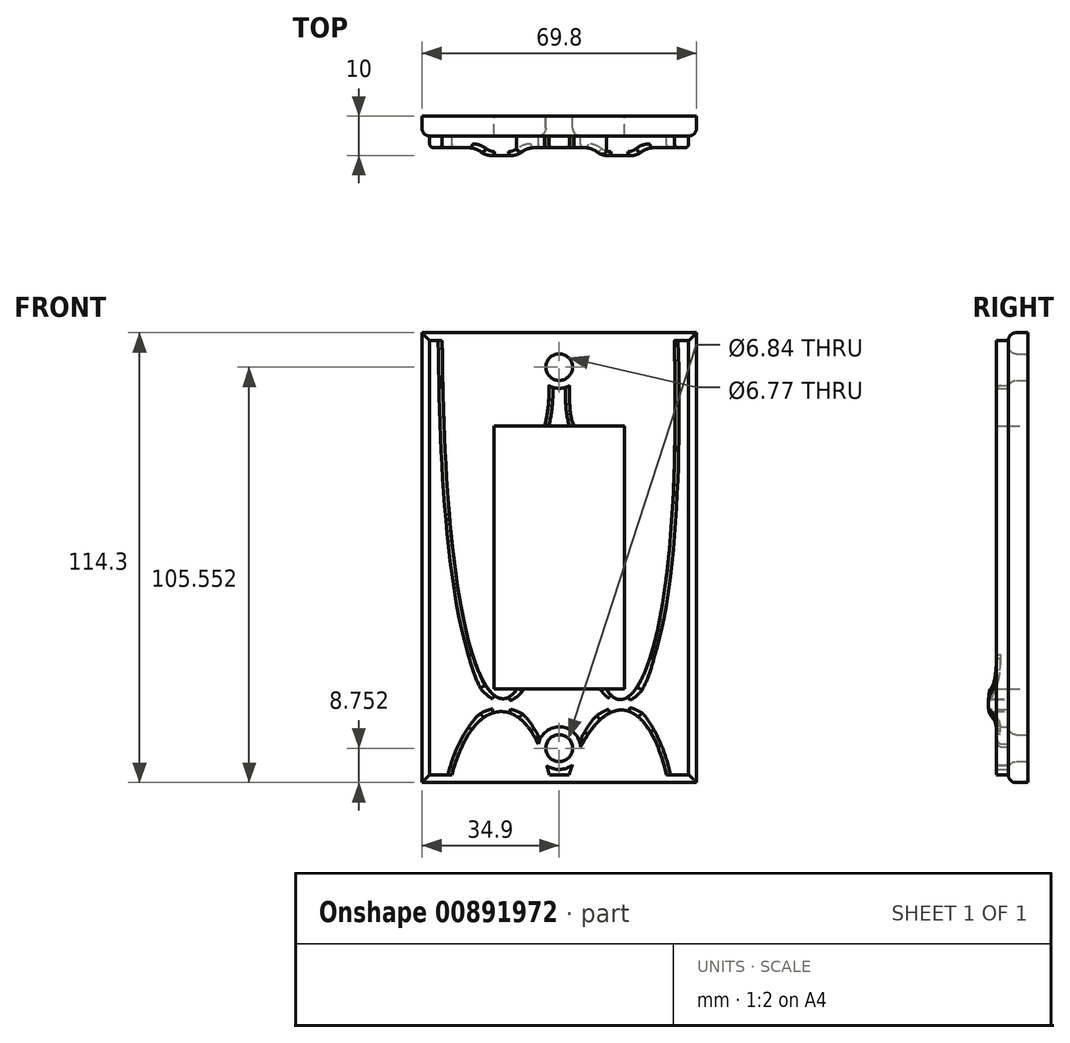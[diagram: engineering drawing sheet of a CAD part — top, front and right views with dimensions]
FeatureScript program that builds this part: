
annotation { "Feature Type Name" : "Feature", "Feature Type Description" : "" }
export const myFeature = defineFeature(function(context is Context, id is Id, definition is map)
    precondition{}
    {
        {
            var Q0;
            Q0=qCreatedBy(makeId("Front.planeOp"),FACE);
            var sketch = newSketch(context, id + "F0", { "sketchPlane" : qUnion([Q0])});
            skLineSegment(sketch, "E0.bottom", {"start": v(-34.9, 67.2) * mm, "end": v(34.9, 67.2) * mm});
            skLineSegment(sketch, "E0.top", {"start": v(-34.9, -47.1) * mm, "end": v(34.9, -47.1) * mm});
            skLineSegment(sketch, "E0.left", {"start": v(-34.9, 67.2) * mm, "end": v(-34.9, -47.1) * mm});
            skLineSegment(sketch, "E0.right", {"start": v(34.9, 67.2) * mm, "end": v(34.9, -47.1) * mm});
            skLineSegment(sketch, "E1", {"start": v(34.9, 67.2) * mm, "end": v(0, 67.2) * mm, "construction": true});
            skLineSegment(sketch, "E2", {"start": v(34.9, 67.2) * mm, "end": v(34.9, 10.05) * mm, "construction": true});
            skLineSegment(sketch, "E3", {"start": v(34.9, 10.05) * mm, "end": v(-34.9, 10.05) * mm, "construction": true});
            skLineSegment(sketch, "E4", {"start": v(-34.9, 10.05) * mm, "end": v(0, 10.05) * mm, "construction": true});
            skLineSegment(sketch, "E5", {"start": v(0, 10.05) * mm, "end": v(0, -47.1) * mm, "construction": true});
            skLineSegment(sketch, "E6", {"start": v(0, -47.1) * mm, "end": v(0, 67.2) * mm, "construction": true});
            skLineSegment(sketch, "E7", {"start": v(0, 10.05) * mm, "end": v(0, 58.45) * mm, "construction": true});
            skLineSegment(sketch, "E8", {"start": v(0, 10.05) * mm, "end": v(0, -38.35) * mm, "construction": true});
            skCircle(sketch, "E9", {"center": v(0, -38.35) * mm, "radius": 3.42 * mm});
            skCircle(sketch, "E10", {"center": v(0, 58.45) * mm, "radius": 3.39 * mm});
            skLineSegment(sketch, "E11.bottom", {"start": v(-16.6, 43.45) * mm, "end": v(16.6, 43.45) * mm});
            skLineSegment(sketch, "E11.top", {"start": v(-16.6, -23.35) * mm, "end": v(16.6, -23.35) * mm});
            skLineSegment(sketch, "E11.left", {"start": v(-16.6, 43.45) * mm, "end": v(-16.6, -23.35) * mm});
            skLineSegment(sketch, "E11.right", {"start": v(16.6, 43.45) * mm, "end": v(16.6, -23.35) * mm});
            skSolve(sketch);
        }
        {
            var Q0;
            Q0=makeQuery(id+"F0.imprint","IMPRINT",FACE,{"disambiguationData":[TD([[makeQuery(id+"F0.imprint","IMPRINT",EDGE,{"derivedFrom":sQuery(id+"F0.wireOp",EDGE,"E0.bottom")}),-1.0]])]});
            extrude(context, id + "F1", {"entities" : qUnion([Q0]), "depth" : 5 * mm, "offsetDistance" : 25 * mm});
        }
        {
            var Q0;
            Q0=makeQuery(id+"F1.opExtrude","CAP_EDGE",EDGE,{"disambiguationData":[OSD([sQuery(id+"F0.wireOp",EDGE,"E0.left")])],"isStart":false});
            var Q1;
            Q1=makeQuery(id+"F1.opExtrude","CAP_EDGE",EDGE,{"disambiguationData":[OSD([sQuery(id+"F0.wireOp",EDGE,"E0.top")])],"isStart":false});
            var Q2;
            Q2=makeQuery(id+"F1.opExtrude","CAP_EDGE",EDGE,{"disambiguationData":[OSD([sQuery(id+"F0.wireOp",EDGE,"E0.right")])],"isStart":false});
            var Q3;
            Q3=makeQuery(id+"F1.opExtrude","CAP_EDGE",EDGE,{"disambiguationData":[OSD([sQuery(id+"F0.wireOp",EDGE,"E0.bottom")])],"isStart":false});
            var Q4;
            Q4=makeQuery(id+"F1.opExtrude","CAP_EDGE",EDGE,{"disambiguationData":[OSD([sQuery(id+"F0.wireOp",EDGE,"E10")])],"isStart":false});
            var Q5;
            Q5=makeQuery(id+"F1.opExtrude","CAP_EDGE",EDGE,{"disambiguationData":[OSD([sQuery(id+"F0.wireOp",EDGE,"E9")])],"isStart":false});
            fillet(context, id + "F2", {"entities" : qUnion([Q0, Q1, Q2, Q3, Q4, Q5]), "radius" : 2 * mm, "tangentPropagation" : true, "allowEdgeOverflow" : false});
        }
        {
            var Q0;
            Q0=makeQuery(id+"F1.opExtrude","CAP_FACE",FACE,{"disambiguationData":[OSD([sQuery(id+"F0.wireOp",EDGE,"E0.bottom"),sQuery(id+"F0.wireOp",EDGE,"E0.top"),sQuery(id+"F0.wireOp",EDGE,"E0.left"),sQuery(id+"F0.wireOp",EDGE,"E0.right"),sQuery(id+"F0.wireOp",EDGE,"E9"),sQuery(id+"F0.wireOp",EDGE,"E10"),sQuery(id+"F0.wireOp",EDGE,"E11.bottom"),sQuery(id+"F0.wireOp",EDGE,"E11.top"),sQuery(id+"F0.wireOp",EDGE,"E11.left"),sQuery(id+"F0.wireOp",EDGE,"E11.right")])],"isStart":false});
            var sketch = newSketch(context, id + "F3", { "sketchPlane" : qUnion([Q0])});
            skLineSegment(sketch, "E12", {"start": v(-33.36, 65.88) * mm, "end": v(-32.9, -45.1) * mm});
            skLineSegment(sketch, "E13", {"start": v(-32.9, -45.1) * mm, "end": v(32.9, -45.1) * mm});
            skLineSegment(sketch, "E14", {"start": v(32.9, -45.1) * mm, "end": v(32.91, 64.93) * mm});
            skPoint(sketch, "E15.2.internal.snap0", {"position": v(0, 43.45) * mm});
            skFitSpline(sketch, "E16", {"points": [v(0, 53.07) * mm, v(15.96, -25.97) * mm, v(29.23, 65.2) * mm], "startDerivative": vector(30.16, -374.7) * mm, "endDerivative": vector(-10.17, 378.6) * mm});
            skFitSpline(sketch, "E17", {"points": [v(-29.73, 65.2) * mm, v(-14.8, -25.74) * mm, v(0, 53.07) * mm], "startDerivative": vector(3.07, -378.06) * mm, "endDerivative": vector(19.08, 378.27) * mm});
            skFitSpline(sketch, "E18", {"points": [v(-27.27, -45.1) * mm, v(-14.8, -29.05) * mm, v(-2.5, -45.1) * mm], "startDerivative": vector(17.97, 66.24) * mm, "endDerivative": vector(18.22, -67.46) * mm});
            skFitSpline(sketch, "E19", {"points": [v(27.28, -45.1) * mm, v(15.96, -28.65) * mm, v(2.5, -45.1) * mm], "startDerivative": vector(-14.59, 62.05) * mm, "endDerivative": vector(-20.48, -61.71) * mm});
            skFitSpline(sketch, "E20", {"points": [v(-3.8, 43.45) * mm, v(-2.61, 53.74) * mm], "startDerivative": vector(2.25, 5.58) * mm, "endDerivative": vector(-0.52, 10.92) * mm});
            skFitSpline(sketch, "E21", {"points": [v(3.8, 43.45) * mm, v(2.61, 53.74) * mm], "startDerivative": vector(-3.3, 6.36) * mm, "endDerivative": vector(0.26, 12.75) * mm});
            skSolve(sketch);
        }
        {
            var Q0;
            {var subQ9=sQuery(id+"F3.wireOp",EDGE,"E14");Q0=makeQuery(id+"F3.imprint","IMPRINT",FACE,{"disambiguationData":[TD([[makeQuery(id+"F3.imprint","IMPRINT",EDGE,{"derivedFrom":subQ9}),1.0]])]});}
            var Q1;
            {var subQ0=sQuery(id+"F3.wireOp",EDGE,"E18");var subQ1=sQuery(id+"F3.wireOp",EDGE,"E13");var subQ2=makeQuery(id+"F3.imprint","INTERSECT",VERTEX,{"disambiguationData":[OD(1.0)],"derivedFrom":[subQ1,subQ0]});Q1=makeQuery(id+"F3.imprint","IMPRINT",FACE,{"disambiguationData":[TD([[makeQuery(id+"F3.imprint","IMPRINT",EDGE,{"disambiguationData":[TD([[subQ2,-1.0]])],"derivedFrom":subQ1}),1.0]])]});}
            var Q2;
            {var subQ0=sQuery(id+"F0.wireOp",EDGE,"E11.top");var subQ10=sQuery(id+"F3.wireOp",EDGE,"E16");var subQ11=makeQuery(id+"F1.opExtrude","CAP_EDGE",EDGE,{"disambiguationData":[OSD([subQ0])],"isStart":false});var subQ12=makeQuery(id+"F3.imprint","INTERSECT",VERTEX,{"derivedFrom":[subQ11,subQ10]});Q2=makeQuery(id+"F3.imprint","IMPRINT",FACE,{"disambiguationData":[TD([[makeQuery(id+"F3.imprint","IMPRINT",EDGE,{"disambiguationData":[TD([[subQ12,1.0]])],"derivedFrom":subQ11}),-1.0]])]});}
            var Q3;
            {var subQ7=sQuery(id+"F3.wireOp",EDGE,"E20");Q3=makeQuery(id+"F3.imprint","IMPRINT",FACE,{"disambiguationData":[TD([[makeQuery(id+"F3.imprint","IMPRINT",EDGE,{"derivedFrom":subQ7}),-1.0]])]});}
            var Q4;
            {var subQ7=sQuery(id+"F3.wireOp",EDGE,"E21");Q4=makeQuery(id+"F3.imprint","IMPRINT",FACE,{"disambiguationData":[TD([[makeQuery(id+"F3.imprint","IMPRINT",EDGE,{"derivedFrom":subQ7}),1.0]])]});}
            var Q5;
            {var subQ1=sQuery(id+"F3.wireOp",EDGE,"E16");var subQ2=sQuery(id+"F0.wireOp",EDGE,"E11.bottom");var subQ5=makeQuery(id+"F1.opExtrude","CAP_EDGE",EDGE,{"disambiguationData":[OSD([subQ2])],"isStart":false});var subQ6=makeQuery(id+"F3.imprint","INTERSECT",VERTEX,{"derivedFrom":[subQ5,subQ1]});Q5=makeQuery(id+"F3.imprint","IMPRINT",FACE,{"disambiguationData":[TD([[makeQuery(id+"F3.imprint","IMPRINT",EDGE,{"disambiguationData":[TD([[subQ6,1.0]])],"derivedFrom":subQ5}),1.0]])]});}
            extrude(context, id + "F4", {"entities" : qUnion([Q0, Q1, Q2, Q3, Q4, Q5]), "operationType" : NewBodyOperationType.ADD, "depth" : 3 * mm, "offsetDistance" : 25 * mm});
        }
        {
            var Q0;
            Q0=makeQuery(id+"F4.opExtrude","CAP_FACE",FACE,{"disambiguationData":[OSD([sQuery(id+"F0.wireOp",EDGE,"E0.bottom"),sQuery(id+"F0.wireOp",EDGE,"E0.top"),sQuery(id+"F0.wireOp",EDGE,"E0.left"),sQuery(id+"F0.wireOp",EDGE,"E0.right"),sQuery(id+"F0.wireOp",EDGE,"E9"),sQuery(id+"F0.wireOp",EDGE,"E10"),sQuery(id+"F0.wireOp",EDGE,"E11.bottom"),sQuery(id+"F0.wireOp",EDGE,"E11.top"),sQuery(id+"F0.wireOp",EDGE,"E11.left"),sQuery(id+"F0.wireOp",EDGE,"E11.right"),sQuery(id+"F3.wireOp",EDGE,"E13"),sQuery(id+"F3.wireOp",EDGE,"E16"),sQuery(id+"F3.wireOp",EDGE,"E17"),sQuery(id+"F3.wireOp",EDGE,"E18"),sQuery(id+"F3.wireOp",EDGE,"E19")])],"isStart":false});
            var sketch = newSketch(context, id + "F5", { "sketchPlane" : qUnion([Q0])});
            skLineSegment(sketch, "E22", {"start": v(-24.07, -6.77) * mm, "end": v(-24.07, -36.63) * mm});
            skLineSegment(sketch, "E23", {"start": v(-5.31, -37.28) * mm, "end": v(-5.31, -23.35) * mm});
            skLineSegment(sketch, "E24", {"start": v(5.41, -38.06) * mm, "end": v(5.41, -23.35) * mm});
            skLineSegment(sketch, "E25", {"start": v(25.07, -38.06) * mm, "end": v(25.07, -7.85) * mm});
            skSolve(sketch);
        }
        {
            var Q0;
            Q0 = qSketchRegion(id + "F5", true);
            var Q1;
            {var subQ4=sQuery(id+"F5.wireOp",EDGE,"E22");Q1=makeQuery(id+"F5.imprint","IMPRINT",FACE,{"disambiguationData":[TD([[makeQuery(id+"F5.imprint","IMPRINT",EDGE,{"derivedFrom":subQ4}),1.0]])]});}
            var Q2;
            {var subQ0=sQuery(id+"F5.wireOp",EDGE,"E24");Q2=makeQuery(id+"F5.imprint","IMPRINT",FACE,{"disambiguationData":[TD([[makeQuery(id+"F5.imprint","IMPRINT",EDGE,{"derivedFrom":subQ0}),-1.0]])]});}
            extrude(context, id + "F6", {"entities" : qUnion([Q0, Q1, Q2]), "operationType" : NewBodyOperationType.ADD, "depth" : 2 * mm, "offsetDistance" : 25 * mm});
        }
        {
            var Q0;
            Q0=makeQuery(id+"F6.opExtrude","CAP_EDGE",EDGE,{"disambiguationData":[OSD([sQuery(id+"F5.wireOp",EDGE,"E22")])],"isStart":false});
            var Q1;
            Q1=makeQuery(id+"F6.opExtrude","CAP_EDGE",EDGE,{"disambiguationData":[OSD([sQuery(id+"F5.wireOp",EDGE,"E23")])],"isStart":false});
            var Q2;
            Q2=makeQuery(id+"F6.opExtrude","CAP_EDGE",EDGE,{"disambiguationData":[OSD([sQuery(id+"F5.wireOp",EDGE,"E24")])],"isStart":false});
            var Q3;
            Q3=makeQuery(id+"F6.opExtrude","CAP_EDGE",EDGE,{"disambiguationData":[OSD([sQuery(id+"F5.wireOp",EDGE,"E25")])],"isStart":false});
            chamfer(context, id + "F7", {"entities" : qUnion([Q0, Q1, Q2, Q3]), "width" : 5 * mm, "tangentPropagation" : true});
        }
        {
            var Q0;
            {var subQ0=sQuery(id+"F5.wireOp",EDGE,"E22");Q0=makeQuery(id+"F7.opChamfer","BLEND_EDGE",EDGE,{"blendedFrom":[makeQuery(id+"F6.opExtrude","CAP_EDGE",EDGE,{"disambiguationData":[OSD([subQ0])],"isStart":false}),makeQuery(id+"F6.opExtrude","CAP_FACE",FACE,{"disambiguationData":[OSD([sQuery(id+"F0.wireOp",EDGE,"E11.top"),sQuery(id+"F3.wireOp",EDGE,"E17"),sQuery(id+"F3.wireOp",EDGE,"E18"),subQ0,sQuery(id+"F5.wireOp",EDGE,"E23")])],"isStart":false})],"blendedInto":[makeQuery(id+"F6.opExtrude","CAP_FACE",FACE,{"disambiguationData":[OSD([sQuery(id+"F0.wireOp",EDGE,"E11.top"),sQuery(id+"F3.wireOp",EDGE,"E17"),sQuery(id+"F3.wireOp",EDGE,"E18"),subQ0,sQuery(id+"F5.wireOp",EDGE,"E23")])],"isStart":false})]});}
            var Q1;
            {var subQ0=sQuery(id+"F5.wireOp",EDGE,"E23");Q1=makeQuery(id+"F7.opChamfer","BLEND_EDGE",EDGE,{"blendedFrom":[makeQuery(id+"F6.opExtrude","CAP_EDGE",EDGE,{"disambiguationData":[OSD([subQ0])],"isStart":false}),makeQuery(id+"F6.opExtrude","CAP_FACE",FACE,{"disambiguationData":[OSD([sQuery(id+"F0.wireOp",EDGE,"E11.top"),sQuery(id+"F3.wireOp",EDGE,"E17"),sQuery(id+"F3.wireOp",EDGE,"E18"),sQuery(id+"F5.wireOp",EDGE,"E22"),subQ0])],"isStart":false})],"blendedInto":[makeQuery(id+"F6.opExtrude","CAP_FACE",FACE,{"disambiguationData":[OSD([sQuery(id+"F0.wireOp",EDGE,"E11.top"),sQuery(id+"F3.wireOp",EDGE,"E17"),sQuery(id+"F3.wireOp",EDGE,"E18"),sQuery(id+"F5.wireOp",EDGE,"E22"),subQ0])],"isStart":false})]});}
            var Q2;
            {var subQ0=sQuery(id+"F5.wireOp",EDGE,"E24");Q2=makeQuery(id+"F7.opChamfer","BLEND_EDGE",EDGE,{"blendedFrom":[makeQuery(id+"F6.opExtrude","CAP_EDGE",EDGE,{"disambiguationData":[OSD([subQ0])],"isStart":false}),makeQuery(id+"F6.opExtrude","CAP_FACE",FACE,{"disambiguationData":[OSD([sQuery(id+"F0.wireOp",EDGE,"E11.top"),sQuery(id+"F3.wireOp",EDGE,"E16"),sQuery(id+"F3.wireOp",EDGE,"E19"),subQ0,sQuery(id+"F5.wireOp",EDGE,"E25")])],"isStart":false})],"blendedInto":[makeQuery(id+"F6.opExtrude","CAP_FACE",FACE,{"disambiguationData":[OSD([sQuery(id+"F0.wireOp",EDGE,"E11.top"),sQuery(id+"F3.wireOp",EDGE,"E16"),sQuery(id+"F3.wireOp",EDGE,"E19"),subQ0,sQuery(id+"F5.wireOp",EDGE,"E25")])],"isStart":false})]});}
            var Q3;
            {var subQ0=sQuery(id+"F5.wireOp",EDGE,"E25");Q3=makeQuery(id+"F7.opChamfer","BLEND_EDGE",EDGE,{"blendedFrom":[makeQuery(id+"F6.opExtrude","CAP_EDGE",EDGE,{"disambiguationData":[OSD([subQ0])],"isStart":false}),makeQuery(id+"F6.opExtrude","CAP_FACE",FACE,{"disambiguationData":[OSD([sQuery(id+"F0.wireOp",EDGE,"E11.top"),sQuery(id+"F3.wireOp",EDGE,"E16"),sQuery(id+"F3.wireOp",EDGE,"E19"),sQuery(id+"F5.wireOp",EDGE,"E24"),subQ0])],"isStart":false})],"blendedInto":[makeQuery(id+"F6.opExtrude","CAP_FACE",FACE,{"disambiguationData":[OSD([sQuery(id+"F0.wireOp",EDGE,"E11.top"),sQuery(id+"F3.wireOp",EDGE,"E16"),sQuery(id+"F3.wireOp",EDGE,"E19"),sQuery(id+"F5.wireOp",EDGE,"E24"),subQ0])],"isStart":false})]});}
            fillet(context, id + "F8", {"entities" : qUnion([Q0, Q1, Q2, Q3]), "radius" : 5 * mm, "tangentPropagation" : true, "allowEdgeOverflow" : false});
        }
        {
            var Q0;
            {var subQ0=sQuery(id+"F0.wireOp",EDGE,"E11.right");var subQ1=sQuery(id+"F0.wireOp",EDGE,"E11.left");var subQ2=sQuery(id+"F0.wireOp",EDGE,"E11.top");var subQ3=sQuery(id+"F0.wireOp",EDGE,"E11.bottom");var subQ4=sQuery(id+"F0.wireOp",EDGE,"E10");var subQ5=sQuery(id+"F0.wireOp",EDGE,"E9");var subQ6=sQuery(id+"F0.wireOp",EDGE,"E0.right");var subQ7=sQuery(id+"F0.wireOp",EDGE,"E0.left");var subQ8=sQuery(id+"F0.wireOp",EDGE,"E0.top");var subQ9=sQuery(id+"F0.wireOp",EDGE,"E0.bottom");var subQ12=sQuery(id+"F3.wireOp",EDGE,"E18");var subQ13=sQuery(id+"F3.wireOp",EDGE,"E13");var subQ15=sQuery(id+"F3.wireOp",EDGE,"E17");var subQ17=sQuery(id+"F5.wireOp",EDGE,"E22");Q0=makeQuery(id+"F7.opChamfer","BLEND_EDGE",EDGE,{"blendedFrom":[makeQuery(id+"F6.opExtrude","CAP_EDGE",EDGE,{"disambiguationData":[OSD([subQ17])],"isStart":false}),makeQuery(id+"F6.boolean.opBoolean","SPLIT",FACE,{"disambiguationData":[TD([makeQuery(id+"F4.opExtrude","SWEPT_FACE",FACE,{"disambiguationData":[OSD([subQ15])]})])],"derivedFrom":makeQuery(id+"F4.opExtrude","CAP_FACE",FACE,{"disambiguationData":[OSD([subQ9,subQ8,subQ7,subQ6,subQ5,subQ4,subQ3,subQ2,subQ1,subQ0,subQ13,sQuery(id+"F3.wireOp",EDGE,"E16"),subQ15,subQ12,sQuery(id+"F3.wireOp",EDGE,"E19")])],"isStart":false})})],"blendedInto":[makeQuery(id+"F6.boolean.opBoolean","SPLIT",FACE,{"disambiguationData":[TD([makeQuery(id+"F4.opExtrude","SWEPT_FACE",FACE,{"disambiguationData":[OSD([subQ15])]})])],"derivedFrom":makeQuery(id+"F4.opExtrude","CAP_FACE",FACE,{"disambiguationData":[OSD([subQ9,subQ8,subQ7,subQ6,subQ5,subQ4,subQ3,subQ2,subQ1,subQ0,subQ13,sQuery(id+"F3.wireOp",EDGE,"E16"),subQ15,subQ12,sQuery(id+"F3.wireOp",EDGE,"E19")])],"isStart":false})})]});}
            var Q1;
            {var subQ0=sQuery(id+"F0.wireOp",EDGE,"E11.top");var subQ2=sQuery(id+"F3.wireOp",EDGE,"E16");var subQ4=sQuery(id+"F3.wireOp",EDGE,"E19");var subQ5=sQuery(id+"F3.wireOp",EDGE,"E18");var subQ6=sQuery(id+"F0.wireOp",EDGE,"E11.right");var subQ7=sQuery(id+"F0.wireOp",EDGE,"E11.left");var subQ8=sQuery(id+"F0.wireOp",EDGE,"E11.bottom");var subQ9=sQuery(id+"F0.wireOp",EDGE,"E10");var subQ10=sQuery(id+"F0.wireOp",EDGE,"E9");var subQ11=sQuery(id+"F0.wireOp",EDGE,"E0.right");var subQ12=sQuery(id+"F0.wireOp",EDGE,"E0.left");var subQ13=sQuery(id+"F0.wireOp",EDGE,"E0.top");var subQ14=sQuery(id+"F0.wireOp",EDGE,"E0.bottom");var subQ18=sQuery(id+"F5.wireOp",EDGE,"E23");var subQ19=sQuery(id+"F3.wireOp",EDGE,"E13");var subQ20=sQuery(id+"F3.wireOp",EDGE,"E17");Q1=makeQuery(id+"F7.opChamfer","BLEND_EDGE",EDGE,{"blendedFrom":[makeQuery(id+"F6.opExtrude","CAP_EDGE",EDGE,{"disambiguationData":[OSD([subQ18])],"isStart":false}),makeQuery(id+"F6.boolean.opBoolean","SPLIT",FACE,{"disambiguationData":[TD([makeQuery(id+"F1.opExtrude","SWEPT_FACE",FACE,{"disambiguationData":[OSD([subQ0])]})])],"derivedFrom":makeQuery(id+"F4.opExtrude","CAP_FACE",FACE,{"disambiguationData":[OSD([subQ14,subQ13,subQ12,subQ11,subQ10,subQ9,subQ8,subQ0,subQ7,subQ6,subQ19,subQ2,subQ20,subQ5,subQ4])],"isStart":false})})],"blendedInto":[makeQuery(id+"F6.boolean.opBoolean","SPLIT",FACE,{"disambiguationData":[TD([makeQuery(id+"F1.opExtrude","SWEPT_FACE",FACE,{"disambiguationData":[OSD([subQ0])]})])],"derivedFrom":makeQuery(id+"F4.opExtrude","CAP_FACE",FACE,{"disambiguationData":[OSD([subQ14,subQ13,subQ12,subQ11,subQ10,subQ9,subQ8,subQ0,subQ7,subQ6,subQ19,subQ2,subQ20,subQ5,subQ4])],"isStart":false})})]});}
            var Q2;
            {var subQ0=sQuery(id+"F0.wireOp",EDGE,"E11.top");var subQ2=sQuery(id+"F3.wireOp",EDGE,"E16");var subQ3=sQuery(id+"F5.wireOp",EDGE,"E24");var subQ4=sQuery(id+"F3.wireOp",EDGE,"E19");var subQ5=sQuery(id+"F3.wireOp",EDGE,"E18");var subQ6=sQuery(id+"F0.wireOp",EDGE,"E11.right");var subQ7=sQuery(id+"F0.wireOp",EDGE,"E11.left");var subQ8=sQuery(id+"F0.wireOp",EDGE,"E11.bottom");var subQ9=sQuery(id+"F0.wireOp",EDGE,"E10");var subQ10=sQuery(id+"F0.wireOp",EDGE,"E9");var subQ11=sQuery(id+"F0.wireOp",EDGE,"E0.right");var subQ12=sQuery(id+"F0.wireOp",EDGE,"E0.left");var subQ13=sQuery(id+"F0.wireOp",EDGE,"E0.top");var subQ14=sQuery(id+"F0.wireOp",EDGE,"E0.bottom");var subQ19=sQuery(id+"F3.wireOp",EDGE,"E13");var subQ20=sQuery(id+"F3.wireOp",EDGE,"E17");Q2=makeQuery(id+"F7.opChamfer","BLEND_EDGE",EDGE,{"blendedFrom":[makeQuery(id+"F6.opExtrude","CAP_EDGE",EDGE,{"disambiguationData":[OSD([subQ3])],"isStart":false}),makeQuery(id+"F6.boolean.opBoolean","SPLIT",FACE,{"disambiguationData":[TD([makeQuery(id+"F1.opExtrude","SWEPT_FACE",FACE,{"disambiguationData":[OSD([subQ0])]})])],"derivedFrom":makeQuery(id+"F4.opExtrude","CAP_FACE",FACE,{"disambiguationData":[OSD([subQ14,subQ13,subQ12,subQ11,subQ10,subQ9,subQ8,subQ0,subQ7,subQ6,subQ19,subQ2,subQ20,subQ5,subQ4])],"isStart":false})})],"blendedInto":[makeQuery(id+"F6.boolean.opBoolean","SPLIT",FACE,{"disambiguationData":[TD([makeQuery(id+"F1.opExtrude","SWEPT_FACE",FACE,{"disambiguationData":[OSD([subQ0])]})])],"derivedFrom":makeQuery(id+"F4.opExtrude","CAP_FACE",FACE,{"disambiguationData":[OSD([subQ14,subQ13,subQ12,subQ11,subQ10,subQ9,subQ8,subQ0,subQ7,subQ6,subQ19,subQ2,subQ20,subQ5,subQ4])],"isStart":false})})]});}
            var Q3;
            {var subQ0=sQuery(id+"F0.wireOp",EDGE,"E11.right");var subQ1=sQuery(id+"F0.wireOp",EDGE,"E11.left");var subQ2=sQuery(id+"F0.wireOp",EDGE,"E11.top");var subQ3=sQuery(id+"F0.wireOp",EDGE,"E11.bottom");var subQ4=sQuery(id+"F0.wireOp",EDGE,"E10");var subQ5=sQuery(id+"F0.wireOp",EDGE,"E9");var subQ6=sQuery(id+"F0.wireOp",EDGE,"E0.right");var subQ7=sQuery(id+"F0.wireOp",EDGE,"E0.left");var subQ8=sQuery(id+"F0.wireOp",EDGE,"E0.top");var subQ9=sQuery(id+"F0.wireOp",EDGE,"E0.bottom");var subQ12=sQuery(id+"F3.wireOp",EDGE,"E16");var subQ13=sQuery(id+"F3.wireOp",EDGE,"E19");var subQ14=sQuery(id+"F3.wireOp",EDGE,"E13");var subQ17=sQuery(id+"F5.wireOp",EDGE,"E25");Q3=makeQuery(id+"F7.opChamfer","BLEND_EDGE",EDGE,{"blendedFrom":[makeQuery(id+"F6.opExtrude","CAP_EDGE",EDGE,{"disambiguationData":[OSD([subQ17])],"isStart":false}),makeQuery(id+"F6.boolean.opBoolean","SPLIT",FACE,{"disambiguationData":[TD([makeQuery(id+"F4.opExtrude","SWEPT_FACE",FACE,{"disambiguationData":[OSD([subQ12])]})])],"derivedFrom":makeQuery(id+"F4.opExtrude","CAP_FACE",FACE,{"disambiguationData":[OSD([subQ9,subQ8,subQ7,subQ6,subQ5,subQ4,subQ3,subQ2,subQ1,subQ0,subQ14,subQ12,sQuery(id+"F3.wireOp",EDGE,"E17"),sQuery(id+"F3.wireOp",EDGE,"E18"),subQ13])],"isStart":false})})],"blendedInto":[makeQuery(id+"F6.boolean.opBoolean","SPLIT",FACE,{"disambiguationData":[TD([makeQuery(id+"F4.opExtrude","SWEPT_FACE",FACE,{"disambiguationData":[OSD([subQ12])]})])],"derivedFrom":makeQuery(id+"F4.opExtrude","CAP_FACE",FACE,{"disambiguationData":[OSD([subQ9,subQ8,subQ7,subQ6,subQ5,subQ4,subQ3,subQ2,subQ1,subQ0,subQ14,subQ12,sQuery(id+"F3.wireOp",EDGE,"E17"),sQuery(id+"F3.wireOp",EDGE,"E18"),subQ13])],"isStart":false})})]});}
            fillet(context, id + "F9", {"entities" : qUnion([Q0, Q1, Q2, Q3]), "radius" : 5 * mm, "tangentPropagation" : true, "allowEdgeOverflow" : false});
        }
        {
            var Q0;
            Q0=makeQuery(id+"F4.opExtrude","CAP_EDGE",EDGE,{"disambiguationData":[OSD([sQuery(id+"F3.wireOp",EDGE,"E16")])],"isStart":false});
            var Q1;
            {var subQ0=sQuery(id+"F3.wireOp",EDGE,"E16");var subQ1=makeQuery(id+"F6.opExtrude","SWEPT_FACE",FACE,{"disambiguationData":[OSD([subQ0])]});var subQ2=makeQuery(id+"F4.opExtrude","SWEPT_FACE",FACE,{"disambiguationData":[OSD([subQ0])]});var subQ3=sQuery(id+"F0.wireOp",EDGE,"E11.right");var subQ4=sQuery(id+"F0.wireOp",EDGE,"E11.left");var subQ5=sQuery(id+"F0.wireOp",EDGE,"E11.top");var subQ6=sQuery(id+"F0.wireOp",EDGE,"E11.bottom");var subQ7=sQuery(id+"F0.wireOp",EDGE,"E10");var subQ8=sQuery(id+"F0.wireOp",EDGE,"E9");var subQ9=sQuery(id+"F0.wireOp",EDGE,"E0.right");var subQ10=sQuery(id+"F0.wireOp",EDGE,"E0.left");var subQ11=sQuery(id+"F0.wireOp",EDGE,"E0.top");var subQ12=sQuery(id+"F0.wireOp",EDGE,"E0.bottom");var subQ15=sQuery(id+"F3.wireOp",EDGE,"E19");var subQ16=sQuery(id+"F3.wireOp",EDGE,"E13");var subQ19=sQuery(id+"F5.wireOp",EDGE,"E25");Q1=makeQuery(id+"F9.opFillet","BLEND_EDGE",EDGE,{"blendedFrom":[makeQuery(id+"F7.opChamfer","BLEND_EDGE",EDGE,{"blendedFrom":[makeQuery(id+"F6.opExtrude","CAP_EDGE",EDGE,{"disambiguationData":[OSD([subQ19])],"isStart":false}),makeQuery(id+"F6.boolean.opBoolean","SPLIT",FACE,{"disambiguationData":[TD([subQ2])],"derivedFrom":makeQuery(id+"F4.opExtrude","CAP_FACE",FACE,{"disambiguationData":[OSD([subQ12,subQ11,subQ10,subQ9,subQ8,subQ7,subQ6,subQ5,subQ4,subQ3,subQ16,subQ0,sQuery(id+"F3.wireOp",EDGE,"E17"),sQuery(id+"F3.wireOp",EDGE,"E18"),subQ15])],"isStart":false})})],"blendedInto":[makeQuery(id+"F6.boolean.opBoolean","SPLIT",FACE,{"disambiguationData":[TD([subQ2])],"derivedFrom":makeQuery(id+"F4.opExtrude","CAP_FACE",FACE,{"disambiguationData":[OSD([subQ12,subQ11,subQ10,subQ9,subQ8,subQ7,subQ6,subQ5,subQ4,subQ3,subQ16,subQ0,sQuery(id+"F3.wireOp",EDGE,"E17"),sQuery(id+"F3.wireOp",EDGE,"E18"),subQ15])],"isStart":false})})]}),makeQuery(id+"F6.boolean.opBoolean","MERGE",FACE,{"derivedFrom":[subQ2,subQ1]})],"blendedInto":[makeQuery(id+"F6.boolean.opBoolean","MERGE",FACE,{"derivedFrom":[subQ2,subQ1]})]});}
            var Q2;
            {var subQ0=sQuery(id+"F3.wireOp",EDGE,"E16");var subQ1=sQuery(id+"F5.wireOp",EDGE,"E25");Q2=makeQuery(id+"F8.opFillet","BLEND_EDGE",EDGE,{"blendedFrom":[makeQuery(id+"F7.opChamfer","BLEND_EDGE",EDGE,{"blendedFrom":[makeQuery(id+"F6.opExtrude","CAP_EDGE",EDGE,{"disambiguationData":[OSD([subQ1])],"isStart":false}),makeQuery(id+"F6.opExtrude","CAP_FACE",FACE,{"disambiguationData":[OSD([sQuery(id+"F0.wireOp",EDGE,"E11.top"),subQ0,sQuery(id+"F3.wireOp",EDGE,"E19"),sQuery(id+"F5.wireOp",EDGE,"E24"),subQ1])],"isStart":false})],"blendedInto":[makeQuery(id+"F6.opExtrude","CAP_FACE",FACE,{"disambiguationData":[OSD([sQuery(id+"F0.wireOp",EDGE,"E11.top"),subQ0,sQuery(id+"F3.wireOp",EDGE,"E19"),sQuery(id+"F5.wireOp",EDGE,"E24"),subQ1])],"isStart":false})]}),makeQuery(id+"F6.boolean.opBoolean","MERGE",FACE,{"derivedFrom":[makeQuery(id+"F4.opExtrude","SWEPT_FACE",FACE,{"disambiguationData":[OSD([subQ0])]}),makeQuery(id+"F6.opExtrude","SWEPT_FACE",FACE,{"disambiguationData":[OSD([subQ0])]})]})],"blendedInto":[makeQuery(id+"F6.boolean.opBoolean","MERGE",FACE,{"derivedFrom":[makeQuery(id+"F4.opExtrude","SWEPT_FACE",FACE,{"disambiguationData":[OSD([subQ0])]}),makeQuery(id+"F6.opExtrude","SWEPT_FACE",FACE,{"disambiguationData":[OSD([subQ0])]})]})]});}
            var Q3;
            Q3=makeQuery(id+"F6.opExtrude","CAP_EDGE",EDGE,{"disambiguationData":[OSD([sQuery(id+"F3.wireOp",EDGE,"E16")])],"isStart":false});
            var Q4;
            {var subQ0=sQuery(id+"F3.wireOp",EDGE,"E16");var subQ1=sQuery(id+"F5.wireOp",EDGE,"E24");Q4=makeQuery(id+"F8.opFillet","BLEND_EDGE",EDGE,{"blendedFrom":[makeQuery(id+"F7.opChamfer","BLEND_EDGE",EDGE,{"blendedFrom":[makeQuery(id+"F6.opExtrude","CAP_EDGE",EDGE,{"disambiguationData":[OSD([subQ1])],"isStart":false}),makeQuery(id+"F6.opExtrude","CAP_FACE",FACE,{"disambiguationData":[OSD([sQuery(id+"F0.wireOp",EDGE,"E11.top"),subQ0,sQuery(id+"F3.wireOp",EDGE,"E19"),subQ1,sQuery(id+"F5.wireOp",EDGE,"E25")])],"isStart":false})],"blendedInto":[makeQuery(id+"F6.opExtrude","CAP_FACE",FACE,{"disambiguationData":[OSD([sQuery(id+"F0.wireOp",EDGE,"E11.top"),subQ0,sQuery(id+"F3.wireOp",EDGE,"E19"),subQ1,sQuery(id+"F5.wireOp",EDGE,"E25")])],"isStart":false})]}),makeQuery(id+"F6.boolean.opBoolean","MERGE",FACE,{"derivedFrom":[makeQuery(id+"F4.opExtrude","SWEPT_FACE",FACE,{"disambiguationData":[OSD([subQ0])]}),makeQuery(id+"F6.opExtrude","SWEPT_FACE",FACE,{"disambiguationData":[OSD([subQ0])]})]})],"blendedInto":[makeQuery(id+"F6.boolean.opBoolean","MERGE",FACE,{"derivedFrom":[makeQuery(id+"F4.opExtrude","SWEPT_FACE",FACE,{"disambiguationData":[OSD([subQ0])]}),makeQuery(id+"F6.opExtrude","SWEPT_FACE",FACE,{"disambiguationData":[OSD([subQ0])]})]})]});}
            var Q5;
            {var subQ0=sQuery(id+"F3.wireOp",EDGE,"E19");Q5=makeQuery(id+"F4.opExtrude","CAP_EDGE",EDGE,{"disambiguationData":[OSD([subQ0]),TDD([makeQuery(id+"F3.imprint","IMPRINT",EDGE,{"disambiguationData":[TD([[makeQuery(id+"F3.imprint","INTERSECT",VERTEX,{"disambiguationData":[OD(0.0)],"derivedFrom":[sQuery(id+"F3.wireOp",EDGE,"E13"),subQ0]}),-1.0]])],"derivedFrom":subQ0})])],"isStart":false});}
            var Q6;
            {var subQ0=sQuery(id+"F3.wireOp",EDGE,"E19");var subQ1=makeQuery(id+"F6.opExtrude","SWEPT_FACE",FACE,{"disambiguationData":[OSD([subQ0])]});var subQ2=sQuery(id+"F3.wireOp",EDGE,"E13");var subQ3=makeQuery(id+"F3.imprint","INTERSECT",VERTEX,{"disambiguationData":[OD(0.0)],"derivedFrom":[subQ2,subQ0]});var subQ4=sQuery(id+"F0.wireOp",EDGE,"E11.right");var subQ5=sQuery(id+"F0.wireOp",EDGE,"E11.left");var subQ6=sQuery(id+"F0.wireOp",EDGE,"E11.top");var subQ7=sQuery(id+"F0.wireOp",EDGE,"E11.bottom");var subQ8=sQuery(id+"F0.wireOp",EDGE,"E10");var subQ9=sQuery(id+"F0.wireOp",EDGE,"E9");var subQ10=sQuery(id+"F0.wireOp",EDGE,"E0.right");var subQ11=sQuery(id+"F0.wireOp",EDGE,"E0.left");var subQ12=sQuery(id+"F0.wireOp",EDGE,"E0.top");var subQ13=sQuery(id+"F0.wireOp",EDGE,"E0.bottom");var subQ15=makeQuery(id+"F4.opExtrude","SWEPT_FACE",FACE,{"disambiguationData":[OSD([subQ0]),TDD([makeQuery(id+"F3.imprint","IMPRINT",EDGE,{"disambiguationData":[TD([[subQ3,-1.0]])],"derivedFrom":subQ0})])]});var subQ17=sQuery(id+"F3.wireOp",EDGE,"E16");var subQ19=sQuery(id+"F5.wireOp",EDGE,"E25");Q6=makeQuery(id+"F9.opFillet","BLEND_EDGE",EDGE,{"blendedFrom":[makeQuery(id+"F7.opChamfer","BLEND_EDGE",EDGE,{"blendedFrom":[makeQuery(id+"F6.opExtrude","CAP_EDGE",EDGE,{"disambiguationData":[OSD([subQ19])],"isStart":false}),makeQuery(id+"F6.boolean.opBoolean","SPLIT",FACE,{"disambiguationData":[TD([makeQuery(id+"F4.opExtrude","SWEPT_FACE",FACE,{"disambiguationData":[OSD([subQ17])]})])],"derivedFrom":makeQuery(id+"F4.opExtrude","CAP_FACE",FACE,{"disambiguationData":[OSD([subQ13,subQ12,subQ11,subQ10,subQ9,subQ8,subQ7,subQ6,subQ5,subQ4,subQ2,subQ17,sQuery(id+"F3.wireOp",EDGE,"E17"),sQuery(id+"F3.wireOp",EDGE,"E18"),subQ0])],"isStart":false})})],"blendedInto":[makeQuery(id+"F6.boolean.opBoolean","SPLIT",FACE,{"disambiguationData":[TD([makeQuery(id+"F4.opExtrude","SWEPT_FACE",FACE,{"disambiguationData":[OSD([subQ17])]})])],"derivedFrom":makeQuery(id+"F4.opExtrude","CAP_FACE",FACE,{"disambiguationData":[OSD([subQ13,subQ12,subQ11,subQ10,subQ9,subQ8,subQ7,subQ6,subQ5,subQ4,subQ2,subQ17,sQuery(id+"F3.wireOp",EDGE,"E17"),sQuery(id+"F3.wireOp",EDGE,"E18"),subQ0])],"isStart":false})})]}),makeQuery(id+"F6.boolean.opBoolean","MERGE",FACE,{"derivedFrom":[subQ15,subQ1]})],"blendedInto":[makeQuery(id+"F6.boolean.opBoolean","MERGE",FACE,{"derivedFrom":[subQ15,subQ1]})]});}
            var Q7;
            {var subQ0=sQuery(id+"F3.wireOp",EDGE,"E19");var subQ1=sQuery(id+"F0.wireOp",EDGE,"E11.top");var subQ3=sQuery(id+"F5.wireOp",EDGE,"E25");Q7=makeQuery(id+"F8.opFillet","BLEND_EDGE",EDGE,{"blendedFrom":[makeQuery(id+"F7.opChamfer","BLEND_EDGE",EDGE,{"blendedFrom":[makeQuery(id+"F6.opExtrude","CAP_EDGE",EDGE,{"disambiguationData":[OSD([subQ3])],"isStart":false}),makeQuery(id+"F6.opExtrude","CAP_FACE",FACE,{"disambiguationData":[OSD([subQ1,sQuery(id+"F3.wireOp",EDGE,"E16"),subQ0,sQuery(id+"F5.wireOp",EDGE,"E24"),subQ3])],"isStart":false})],"blendedInto":[makeQuery(id+"F6.opExtrude","CAP_FACE",FACE,{"disambiguationData":[OSD([subQ1,sQuery(id+"F3.wireOp",EDGE,"E16"),subQ0,sQuery(id+"F5.wireOp",EDGE,"E24"),subQ3])],"isStart":false})]}),makeQuery(id+"F6.boolean.opBoolean","MERGE",FACE,{"derivedFrom":[makeQuery(id+"F4.opExtrude","SWEPT_FACE",FACE,{"disambiguationData":[OSD([subQ0]),TDD([makeQuery(id+"F3.imprint","IMPRINT",EDGE,{"disambiguationData":[TD([[makeQuery(id+"F3.imprint","INTERSECT",VERTEX,{"disambiguationData":[OD(0.0)],"derivedFrom":[sQuery(id+"F3.wireOp",EDGE,"E13"),subQ0]}),-1.0]])],"derivedFrom":subQ0})])]}),makeQuery(id+"F6.opExtrude","SWEPT_FACE",FACE,{"disambiguationData":[OSD([subQ0])]})]})],"blendedInto":[makeQuery(id+"F6.boolean.opBoolean","MERGE",FACE,{"derivedFrom":[makeQuery(id+"F4.opExtrude","SWEPT_FACE",FACE,{"disambiguationData":[OSD([subQ0]),TDD([makeQuery(id+"F3.imprint","IMPRINT",EDGE,{"disambiguationData":[TD([[makeQuery(id+"F3.imprint","INTERSECT",VERTEX,{"disambiguationData":[OD(0.0)],"derivedFrom":[sQuery(id+"F3.wireOp",EDGE,"E13"),subQ0]}),-1.0]])],"derivedFrom":subQ0})])]}),makeQuery(id+"F6.opExtrude","SWEPT_FACE",FACE,{"disambiguationData":[OSD([subQ0])]})]})]});}
            var Q8;
            Q8=makeQuery(id+"F6.opExtrude","CAP_EDGE",EDGE,{"disambiguationData":[OSD([sQuery(id+"F3.wireOp",EDGE,"E19")])],"isStart":false});
            var Q9;
            {var subQ0=sQuery(id+"F3.wireOp",EDGE,"E19");var subQ1=sQuery(id+"F0.wireOp",EDGE,"E11.top");var subQ3=sQuery(id+"F5.wireOp",EDGE,"E24");Q9=makeQuery(id+"F8.opFillet","BLEND_EDGE",EDGE,{"blendedFrom":[makeQuery(id+"F7.opChamfer","BLEND_EDGE",EDGE,{"blendedFrom":[makeQuery(id+"F6.opExtrude","CAP_EDGE",EDGE,{"disambiguationData":[OSD([subQ3])],"isStart":false}),makeQuery(id+"F6.opExtrude","CAP_FACE",FACE,{"disambiguationData":[OSD([subQ1,sQuery(id+"F3.wireOp",EDGE,"E16"),subQ0,subQ3,sQuery(id+"F5.wireOp",EDGE,"E25")])],"isStart":false})],"blendedInto":[makeQuery(id+"F6.opExtrude","CAP_FACE",FACE,{"disambiguationData":[OSD([subQ1,sQuery(id+"F3.wireOp",EDGE,"E16"),subQ0,subQ3,sQuery(id+"F5.wireOp",EDGE,"E25")])],"isStart":false})]}),makeQuery(id+"F6.boolean.opBoolean","MERGE",FACE,{"derivedFrom":[makeQuery(id+"F4.opExtrude","SWEPT_FACE",FACE,{"disambiguationData":[OSD([subQ0]),TDD([makeQuery(id+"F3.imprint","IMPRINT",EDGE,{"disambiguationData":[TD([[makeQuery(id+"F3.imprint","INTERSECT",VERTEX,{"disambiguationData":[OD(0.0)],"derivedFrom":[sQuery(id+"F3.wireOp",EDGE,"E13"),subQ0]}),-1.0]])],"derivedFrom":subQ0})])]}),makeQuery(id+"F6.opExtrude","SWEPT_FACE",FACE,{"disambiguationData":[OSD([subQ0])]})]})],"blendedInto":[makeQuery(id+"F6.boolean.opBoolean","MERGE",FACE,{"derivedFrom":[makeQuery(id+"F4.opExtrude","SWEPT_FACE",FACE,{"disambiguationData":[OSD([subQ0]),TDD([makeQuery(id+"F3.imprint","IMPRINT",EDGE,{"disambiguationData":[TD([[makeQuery(id+"F3.imprint","INTERSECT",VERTEX,{"disambiguationData":[OD(0.0)],"derivedFrom":[sQuery(id+"F3.wireOp",EDGE,"E13"),subQ0]}),-1.0]])],"derivedFrom":subQ0})])]}),makeQuery(id+"F6.opExtrude","SWEPT_FACE",FACE,{"disambiguationData":[OSD([subQ0])]})]})]});}
            var Q10;
            {var subQ0=sQuery(id+"F3.wireOp",EDGE,"E19");var subQ1=makeQuery(id+"F6.opExtrude","SWEPT_FACE",FACE,{"disambiguationData":[OSD([subQ0])]});var subQ2=sQuery(id+"F3.wireOp",EDGE,"E13");var subQ3=sQuery(id+"F0.wireOp",EDGE,"E11.right");var subQ4=sQuery(id+"F0.wireOp",EDGE,"E11.left");var subQ5=sQuery(id+"F0.wireOp",EDGE,"E11.top");var subQ6=sQuery(id+"F0.wireOp",EDGE,"E11.bottom");var subQ7=sQuery(id+"F0.wireOp",EDGE,"E10");var subQ8=sQuery(id+"F0.wireOp",EDGE,"E9");var subQ9=sQuery(id+"F0.wireOp",EDGE,"E0.right");var subQ10=sQuery(id+"F0.wireOp",EDGE,"E0.left");var subQ11=sQuery(id+"F0.wireOp",EDGE,"E0.top");var subQ12=sQuery(id+"F0.wireOp",EDGE,"E0.bottom");var subQ15=makeQuery(id+"F4.opExtrude","SWEPT_FACE",FACE,{"disambiguationData":[OSD([subQ0]),TDD([makeQuery(id+"F3.imprint","IMPRINT",EDGE,{"disambiguationData":[TD([[makeQuery(id+"F3.imprint","INTERSECT",VERTEX,{"disambiguationData":[OD(0.0)],"derivedFrom":[subQ2,subQ0]}),-1.0]])],"derivedFrom":subQ0})])]});var subQ17=sQuery(id+"F3.wireOp",EDGE,"E16");var subQ18=sQuery(id+"F5.wireOp",EDGE,"E24");var subQ19=sQuery(id+"F3.wireOp",EDGE,"E18");var subQ22=sQuery(id+"F3.wireOp",EDGE,"E17");Q10=makeQuery(id+"F9.opFillet","BLEND_EDGE",EDGE,{"blendedFrom":[makeQuery(id+"F7.opChamfer","BLEND_EDGE",EDGE,{"blendedFrom":[makeQuery(id+"F6.opExtrude","CAP_EDGE",EDGE,{"disambiguationData":[OSD([subQ18])],"isStart":false}),makeQuery(id+"F6.boolean.opBoolean","SPLIT",FACE,{"disambiguationData":[TD([makeQuery(id+"F1.opExtrude","SWEPT_FACE",FACE,{"disambiguationData":[OSD([subQ5])]})])],"derivedFrom":makeQuery(id+"F4.opExtrude","CAP_FACE",FACE,{"disambiguationData":[OSD([subQ12,subQ11,subQ10,subQ9,subQ8,subQ7,subQ6,subQ5,subQ4,subQ3,subQ2,subQ17,subQ22,subQ19,subQ0])],"isStart":false})})],"blendedInto":[makeQuery(id+"F6.boolean.opBoolean","SPLIT",FACE,{"disambiguationData":[TD([makeQuery(id+"F1.opExtrude","SWEPT_FACE",FACE,{"disambiguationData":[OSD([subQ5])]})])],"derivedFrom":makeQuery(id+"F4.opExtrude","CAP_FACE",FACE,{"disambiguationData":[OSD([subQ12,subQ11,subQ10,subQ9,subQ8,subQ7,subQ6,subQ5,subQ4,subQ3,subQ2,subQ17,subQ22,subQ19,subQ0])],"isStart":false})})]}),makeQuery(id+"F6.boolean.opBoolean","MERGE",FACE,{"derivedFrom":[subQ15,subQ1]})],"blendedInto":[makeQuery(id+"F6.boolean.opBoolean","MERGE",FACE,{"derivedFrom":[subQ15,subQ1]})]});}
            var Q11;
            {var subQ0=sQuery(id+"F3.wireOp",EDGE,"E19");var subQ1=sQuery(id+"F0.wireOp",EDGE,"E11.right");var subQ2=sQuery(id+"F0.wireOp",EDGE,"E11.left");var subQ3=sQuery(id+"F0.wireOp",EDGE,"E11.top");var subQ4=sQuery(id+"F0.wireOp",EDGE,"E11.bottom");var subQ5=sQuery(id+"F0.wireOp",EDGE,"E10");var subQ6=sQuery(id+"F0.wireOp",EDGE,"E9");var subQ7=sQuery(id+"F0.wireOp",EDGE,"E0.right");var subQ8=sQuery(id+"F0.wireOp",EDGE,"E0.left");var subQ9=sQuery(id+"F0.wireOp",EDGE,"E0.top");var subQ10=sQuery(id+"F0.wireOp",EDGE,"E0.bottom");Q11=makeQuery(id+"F7.opChamfer","TWEAK_EDGE",EDGE,{"derivedFrom":[makeQuery(id+"F6.boolean.opBoolean","MERGE",VERTEX,{"derivedFrom":[makeQuery(id+"F4.opExtrude","CAP_VERTEX",VERTEX,{"disambiguationData":[OSD([subQ10,subQ9,subQ8,subQ7,subQ6,subQ5,subQ4,subQ3,subQ2,subQ1,subQ0]),TDD([makeQuery(id+"F3.imprint","INTERSECT",VERTEX,{"disambiguationData":[OD(0.0)],"derivedFrom":[makeQuery(id+"F2.opFillet","BLEND_EDGE",EDGE,{"blendedFrom":[makeQuery(id+"F1.opExtrude","CAP_EDGE",EDGE,{"disambiguationData":[OSD([subQ6])],"isStart":false}),makeQuery(id+"F1.opExtrude","CAP_FACE",FACE,{"disambiguationData":[OSD([subQ10,subQ9,subQ8,subQ7,subQ6,subQ5,subQ4,subQ3,subQ2,subQ1])],"isStart":false})],"blendedInto":[makeQuery(id+"F1.opExtrude","CAP_FACE",FACE,{"disambiguationData":[OSD([subQ10,subQ9,subQ8,subQ7,subQ6,subQ5,subQ4,subQ3,subQ2,subQ1])],"isStart":false})]}),subQ0]})])],"isStart":false}),makeQuery(id+"F6.opExtrude","CAP_VERTEX",VERTEX,{"disambiguationData":[OSD([subQ10,subQ9,subQ8,subQ7,subQ6,subQ5,subQ4,subQ3,subQ2,subQ1,subQ0,sQuery(id+"F5.wireOp",EDGE,"E24")])],"isStart":true})]})]});}
            var Q12;
            {var subQ0=sQuery(id+"F0.wireOp",EDGE,"E11.right");var subQ1=sQuery(id+"F0.wireOp",EDGE,"E11.left");var subQ2=sQuery(id+"F0.wireOp",EDGE,"E11.top");var subQ3=sQuery(id+"F0.wireOp",EDGE,"E11.bottom");var subQ4=sQuery(id+"F0.wireOp",EDGE,"E10");var subQ5=sQuery(id+"F0.wireOp",EDGE,"E9");var subQ6=sQuery(id+"F0.wireOp",EDGE,"E0.right");var subQ7=sQuery(id+"F0.wireOp",EDGE,"E0.left");var subQ8=sQuery(id+"F0.wireOp",EDGE,"E0.top");var subQ9=sQuery(id+"F0.wireOp",EDGE,"E0.bottom");var subQ10=makeQuery(id+"F2.opFillet","BLEND_EDGE",EDGE,{"blendedFrom":[makeQuery(id+"F1.opExtrude","CAP_EDGE",EDGE,{"disambiguationData":[OSD([subQ5])],"isStart":false}),makeQuery(id+"F1.opExtrude","CAP_FACE",FACE,{"disambiguationData":[OSD([subQ9,subQ8,subQ7,subQ6,subQ5,subQ4,subQ3,subQ2,subQ1,subQ0])],"isStart":false})],"blendedInto":[makeQuery(id+"F1.opExtrude","CAP_FACE",FACE,{"disambiguationData":[OSD([subQ9,subQ8,subQ7,subQ6,subQ5,subQ4,subQ3,subQ2,subQ1,subQ0])],"isStart":false})]});Q12=makeQuery(id+"F4.opExtrude","CAP_EDGE",EDGE,{"disambiguationData":[OSD([subQ9,subQ8,subQ7,subQ6,subQ5,subQ4,subQ3,subQ2,subQ1,subQ0]),TDD([makeQuery(id+"F3.imprint","IMPRINT",EDGE,{"disambiguationData":[TD([[makeQuery(id+"F3.imprint","INTERSECT",VERTEX,{"disambiguationData":[OD(0.0)],"derivedFrom":[subQ10,sQuery(id+"F3.wireOp",EDGE,"E18")]}),-1.0]])],"derivedFrom":subQ10})])],"isStart":false});}
            var Q13;
            {var subQ0=sQuery(id+"F3.wireOp",EDGE,"E18");var subQ1=sQuery(id+"F0.wireOp",EDGE,"E11.right");var subQ2=sQuery(id+"F0.wireOp",EDGE,"E11.left");var subQ3=sQuery(id+"F0.wireOp",EDGE,"E11.top");var subQ4=sQuery(id+"F0.wireOp",EDGE,"E11.bottom");var subQ5=sQuery(id+"F0.wireOp",EDGE,"E10");var subQ6=sQuery(id+"F0.wireOp",EDGE,"E9");var subQ7=sQuery(id+"F0.wireOp",EDGE,"E0.right");var subQ8=sQuery(id+"F0.wireOp",EDGE,"E0.left");var subQ9=sQuery(id+"F0.wireOp",EDGE,"E0.top");var subQ10=sQuery(id+"F0.wireOp",EDGE,"E0.bottom");Q13=makeQuery(id+"F7.opChamfer","TWEAK_EDGE",EDGE,{"derivedFrom":[makeQuery(id+"F6.boolean.opBoolean","MERGE",VERTEX,{"derivedFrom":[makeQuery(id+"F4.opExtrude","CAP_VERTEX",VERTEX,{"disambiguationData":[OSD([subQ10,subQ9,subQ8,subQ7,subQ6,subQ5,subQ4,subQ3,subQ2,subQ1,subQ0]),TDD([makeQuery(id+"F3.imprint","INTERSECT",VERTEX,{"disambiguationData":[OD(0.0)],"derivedFrom":[makeQuery(id+"F2.opFillet","BLEND_EDGE",EDGE,{"blendedFrom":[makeQuery(id+"F1.opExtrude","CAP_EDGE",EDGE,{"disambiguationData":[OSD([subQ6])],"isStart":false}),makeQuery(id+"F1.opExtrude","CAP_FACE",FACE,{"disambiguationData":[OSD([subQ10,subQ9,subQ8,subQ7,subQ6,subQ5,subQ4,subQ3,subQ2,subQ1])],"isStart":false})],"blendedInto":[makeQuery(id+"F1.opExtrude","CAP_FACE",FACE,{"disambiguationData":[OSD([subQ10,subQ9,subQ8,subQ7,subQ6,subQ5,subQ4,subQ3,subQ2,subQ1])],"isStart":false})]}),subQ0]})])],"isStart":false}),makeQuery(id+"F6.opExtrude","CAP_VERTEX",VERTEX,{"disambiguationData":[OSD([subQ10,subQ9,subQ8,subQ7,subQ6,subQ5,subQ4,subQ3,subQ2,subQ1,subQ0,sQuery(id+"F5.wireOp",EDGE,"E23")])],"isStart":true})]})]});}
            var Q14;
            {var subQ0=sQuery(id+"F3.wireOp",EDGE,"E18");var subQ1=makeQuery(id+"F6.opExtrude","SWEPT_FACE",FACE,{"disambiguationData":[OSD([subQ0])]});var subQ2=sQuery(id+"F3.wireOp",EDGE,"E13");var subQ3=sQuery(id+"F0.wireOp",EDGE,"E11.right");var subQ4=sQuery(id+"F0.wireOp",EDGE,"E11.left");var subQ5=sQuery(id+"F0.wireOp",EDGE,"E11.top");var subQ6=sQuery(id+"F0.wireOp",EDGE,"E11.bottom");var subQ7=sQuery(id+"F0.wireOp",EDGE,"E10");var subQ8=sQuery(id+"F0.wireOp",EDGE,"E9");var subQ9=sQuery(id+"F0.wireOp",EDGE,"E0.right");var subQ10=sQuery(id+"F0.wireOp",EDGE,"E0.left");var subQ11=sQuery(id+"F0.wireOp",EDGE,"E0.top");var subQ12=sQuery(id+"F0.wireOp",EDGE,"E0.bottom");var subQ15=makeQuery(id+"F4.opExtrude","SWEPT_FACE",FACE,{"disambiguationData":[OSD([subQ0]),TDD([makeQuery(id+"F3.imprint","IMPRINT",EDGE,{"disambiguationData":[TD([[makeQuery(id+"F3.imprint","INTERSECT",VERTEX,{"disambiguationData":[OD(0.0)],"derivedFrom":[subQ2,subQ0]}),-1.0]])],"derivedFrom":subQ0})])]});var subQ17=sQuery(id+"F3.wireOp",EDGE,"E16");var subQ19=sQuery(id+"F3.wireOp",EDGE,"E19");var subQ21=sQuery(id+"F5.wireOp",EDGE,"E23");var subQ22=sQuery(id+"F3.wireOp",EDGE,"E17");Q14=makeQuery(id+"F9.opFillet","BLEND_EDGE",EDGE,{"blendedFrom":[makeQuery(id+"F7.opChamfer","BLEND_EDGE",EDGE,{"blendedFrom":[makeQuery(id+"F6.opExtrude","CAP_EDGE",EDGE,{"disambiguationData":[OSD([subQ21])],"isStart":false}),makeQuery(id+"F6.boolean.opBoolean","SPLIT",FACE,{"disambiguationData":[TD([makeQuery(id+"F1.opExtrude","SWEPT_FACE",FACE,{"disambiguationData":[OSD([subQ5])]})])],"derivedFrom":makeQuery(id+"F4.opExtrude","CAP_FACE",FACE,{"disambiguationData":[OSD([subQ12,subQ11,subQ10,subQ9,subQ8,subQ7,subQ6,subQ5,subQ4,subQ3,subQ2,subQ17,subQ22,subQ0,subQ19])],"isStart":false})})],"blendedInto":[makeQuery(id+"F6.boolean.opBoolean","SPLIT",FACE,{"disambiguationData":[TD([makeQuery(id+"F1.opExtrude","SWEPT_FACE",FACE,{"disambiguationData":[OSD([subQ5])]})])],"derivedFrom":makeQuery(id+"F4.opExtrude","CAP_FACE",FACE,{"disambiguationData":[OSD([subQ12,subQ11,subQ10,subQ9,subQ8,subQ7,subQ6,subQ5,subQ4,subQ3,subQ2,subQ17,subQ22,subQ0,subQ19])],"isStart":false})})]}),makeQuery(id+"F6.boolean.opBoolean","MERGE",FACE,{"derivedFrom":[subQ15,subQ1]})],"blendedInto":[makeQuery(id+"F6.boolean.opBoolean","MERGE",FACE,{"derivedFrom":[subQ15,subQ1]})]});}
            var Q15;
            {var subQ0=sQuery(id+"F3.wireOp",EDGE,"E18");var subQ1=sQuery(id+"F0.wireOp",EDGE,"E11.top");var subQ3=sQuery(id+"F5.wireOp",EDGE,"E23");Q15=makeQuery(id+"F8.opFillet","BLEND_EDGE",EDGE,{"blendedFrom":[makeQuery(id+"F7.opChamfer","BLEND_EDGE",EDGE,{"blendedFrom":[makeQuery(id+"F6.opExtrude","CAP_EDGE",EDGE,{"disambiguationData":[OSD([subQ3])],"isStart":false}),makeQuery(id+"F6.opExtrude","CAP_FACE",FACE,{"disambiguationData":[OSD([subQ1,sQuery(id+"F3.wireOp",EDGE,"E17"),subQ0,sQuery(id+"F5.wireOp",EDGE,"E22"),subQ3])],"isStart":false})],"blendedInto":[makeQuery(id+"F6.opExtrude","CAP_FACE",FACE,{"disambiguationData":[OSD([subQ1,sQuery(id+"F3.wireOp",EDGE,"E17"),subQ0,sQuery(id+"F5.wireOp",EDGE,"E22"),subQ3])],"isStart":false})]}),makeQuery(id+"F6.boolean.opBoolean","MERGE",FACE,{"derivedFrom":[makeQuery(id+"F4.opExtrude","SWEPT_FACE",FACE,{"disambiguationData":[OSD([subQ0]),TDD([makeQuery(id+"F3.imprint","IMPRINT",EDGE,{"disambiguationData":[TD([[makeQuery(id+"F3.imprint","INTERSECT",VERTEX,{"disambiguationData":[OD(0.0)],"derivedFrom":[sQuery(id+"F3.wireOp",EDGE,"E13"),subQ0]}),-1.0]])],"derivedFrom":subQ0})])]}),makeQuery(id+"F6.opExtrude","SWEPT_FACE",FACE,{"disambiguationData":[OSD([subQ0])]})]})],"blendedInto":[makeQuery(id+"F6.boolean.opBoolean","MERGE",FACE,{"derivedFrom":[makeQuery(id+"F4.opExtrude","SWEPT_FACE",FACE,{"disambiguationData":[OSD([subQ0]),TDD([makeQuery(id+"F3.imprint","IMPRINT",EDGE,{"disambiguationData":[TD([[makeQuery(id+"F3.imprint","INTERSECT",VERTEX,{"disambiguationData":[OD(0.0)],"derivedFrom":[sQuery(id+"F3.wireOp",EDGE,"E13"),subQ0]}),-1.0]])],"derivedFrom":subQ0})])]}),makeQuery(id+"F6.opExtrude","SWEPT_FACE",FACE,{"disambiguationData":[OSD([subQ0])]})]})]});}
            var Q16;
            Q16=makeQuery(id+"F6.opExtrude","CAP_EDGE",EDGE,{"disambiguationData":[OSD([sQuery(id+"F3.wireOp",EDGE,"E18")])],"isStart":false});
            var Q17;
            {var subQ0=sQuery(id+"F3.wireOp",EDGE,"E18");var subQ1=sQuery(id+"F0.wireOp",EDGE,"E11.top");var subQ3=sQuery(id+"F5.wireOp",EDGE,"E22");Q17=makeQuery(id+"F8.opFillet","BLEND_EDGE",EDGE,{"blendedFrom":[makeQuery(id+"F7.opChamfer","BLEND_EDGE",EDGE,{"blendedFrom":[makeQuery(id+"F6.opExtrude","CAP_EDGE",EDGE,{"disambiguationData":[OSD([subQ3])],"isStart":false}),makeQuery(id+"F6.opExtrude","CAP_FACE",FACE,{"disambiguationData":[OSD([subQ1,sQuery(id+"F3.wireOp",EDGE,"E17"),subQ0,subQ3,sQuery(id+"F5.wireOp",EDGE,"E23")])],"isStart":false})],"blendedInto":[makeQuery(id+"F6.opExtrude","CAP_FACE",FACE,{"disambiguationData":[OSD([subQ1,sQuery(id+"F3.wireOp",EDGE,"E17"),subQ0,subQ3,sQuery(id+"F5.wireOp",EDGE,"E23")])],"isStart":false})]}),makeQuery(id+"F6.boolean.opBoolean","MERGE",FACE,{"derivedFrom":[makeQuery(id+"F4.opExtrude","SWEPT_FACE",FACE,{"disambiguationData":[OSD([subQ0]),TDD([makeQuery(id+"F3.imprint","IMPRINT",EDGE,{"disambiguationData":[TD([[makeQuery(id+"F3.imprint","INTERSECT",VERTEX,{"disambiguationData":[OD(0.0)],"derivedFrom":[sQuery(id+"F3.wireOp",EDGE,"E13"),subQ0]}),-1.0]])],"derivedFrom":subQ0})])]}),makeQuery(id+"F6.opExtrude","SWEPT_FACE",FACE,{"disambiguationData":[OSD([subQ0])]})]})],"blendedInto":[makeQuery(id+"F6.boolean.opBoolean","MERGE",FACE,{"derivedFrom":[makeQuery(id+"F4.opExtrude","SWEPT_FACE",FACE,{"disambiguationData":[OSD([subQ0]),TDD([makeQuery(id+"F3.imprint","IMPRINT",EDGE,{"disambiguationData":[TD([[makeQuery(id+"F3.imprint","INTERSECT",VERTEX,{"disambiguationData":[OD(0.0)],"derivedFrom":[sQuery(id+"F3.wireOp",EDGE,"E13"),subQ0]}),-1.0]])],"derivedFrom":subQ0})])]}),makeQuery(id+"F6.opExtrude","SWEPT_FACE",FACE,{"disambiguationData":[OSD([subQ0])]})]})]});}
            var Q18;
            {var subQ0=sQuery(id+"F3.wireOp",EDGE,"E18");var subQ1=makeQuery(id+"F6.opExtrude","SWEPT_FACE",FACE,{"disambiguationData":[OSD([subQ0])]});var subQ2=sQuery(id+"F3.wireOp",EDGE,"E13");var subQ3=makeQuery(id+"F3.imprint","INTERSECT",VERTEX,{"disambiguationData":[OD(0.0)],"derivedFrom":[subQ2,subQ0]});var subQ4=sQuery(id+"F0.wireOp",EDGE,"E11.right");var subQ5=sQuery(id+"F0.wireOp",EDGE,"E11.left");var subQ6=sQuery(id+"F0.wireOp",EDGE,"E11.top");var subQ7=sQuery(id+"F0.wireOp",EDGE,"E11.bottom");var subQ8=sQuery(id+"F0.wireOp",EDGE,"E10");var subQ9=sQuery(id+"F0.wireOp",EDGE,"E9");var subQ10=sQuery(id+"F0.wireOp",EDGE,"E0.right");var subQ11=sQuery(id+"F0.wireOp",EDGE,"E0.left");var subQ12=sQuery(id+"F0.wireOp",EDGE,"E0.top");var subQ13=sQuery(id+"F0.wireOp",EDGE,"E0.bottom");var subQ15=makeQuery(id+"F4.opExtrude","SWEPT_FACE",FACE,{"disambiguationData":[OSD([subQ0]),TDD([makeQuery(id+"F3.imprint","IMPRINT",EDGE,{"disambiguationData":[TD([[subQ3,-1.0]])],"derivedFrom":subQ0})])]});var subQ17=sQuery(id+"F3.wireOp",EDGE,"E17");var subQ19=sQuery(id+"F5.wireOp",EDGE,"E22");Q18=makeQuery(id+"F9.opFillet","BLEND_EDGE",EDGE,{"blendedFrom":[makeQuery(id+"F7.opChamfer","BLEND_EDGE",EDGE,{"blendedFrom":[makeQuery(id+"F6.opExtrude","CAP_EDGE",EDGE,{"disambiguationData":[OSD([subQ19])],"isStart":false}),makeQuery(id+"F6.boolean.opBoolean","SPLIT",FACE,{"disambiguationData":[TD([makeQuery(id+"F4.opExtrude","SWEPT_FACE",FACE,{"disambiguationData":[OSD([subQ17])]})])],"derivedFrom":makeQuery(id+"F4.opExtrude","CAP_FACE",FACE,{"disambiguationData":[OSD([subQ13,subQ12,subQ11,subQ10,subQ9,subQ8,subQ7,subQ6,subQ5,subQ4,subQ2,sQuery(id+"F3.wireOp",EDGE,"E16"),subQ17,subQ0,sQuery(id+"F3.wireOp",EDGE,"E19")])],"isStart":false})})],"blendedInto":[makeQuery(id+"F6.boolean.opBoolean","SPLIT",FACE,{"disambiguationData":[TD([makeQuery(id+"F4.opExtrude","SWEPT_FACE",FACE,{"disambiguationData":[OSD([subQ17])]})])],"derivedFrom":makeQuery(id+"F4.opExtrude","CAP_FACE",FACE,{"disambiguationData":[OSD([subQ13,subQ12,subQ11,subQ10,subQ9,subQ8,subQ7,subQ6,subQ5,subQ4,subQ2,sQuery(id+"F3.wireOp",EDGE,"E16"),subQ17,subQ0,sQuery(id+"F3.wireOp",EDGE,"E19")])],"isStart":false})})]}),makeQuery(id+"F6.boolean.opBoolean","MERGE",FACE,{"derivedFrom":[subQ15,subQ1]})],"blendedInto":[makeQuery(id+"F6.boolean.opBoolean","MERGE",FACE,{"derivedFrom":[subQ15,subQ1]})]});}
            var Q19;
            {var subQ0=sQuery(id+"F3.wireOp",EDGE,"E18");Q19=makeQuery(id+"F4.opExtrude","CAP_EDGE",EDGE,{"disambiguationData":[OSD([subQ0]),TDD([makeQuery(id+"F3.imprint","IMPRINT",EDGE,{"disambiguationData":[TD([[makeQuery(id+"F3.imprint","INTERSECT",VERTEX,{"disambiguationData":[OD(0.0)],"derivedFrom":[sQuery(id+"F3.wireOp",EDGE,"E13"),subQ0]}),-1.0]])],"derivedFrom":subQ0})])],"isStart":false});}
            var Q20;
            {var subQ0=sQuery(id+"F3.wireOp",EDGE,"E17");var subQ1=sQuery(id+"F5.wireOp",EDGE,"E23");Q20=makeQuery(id+"F8.opFillet","BLEND_EDGE",EDGE,{"blendedFrom":[makeQuery(id+"F7.opChamfer","BLEND_EDGE",EDGE,{"blendedFrom":[makeQuery(id+"F6.opExtrude","CAP_EDGE",EDGE,{"disambiguationData":[OSD([subQ1])],"isStart":false}),makeQuery(id+"F6.opExtrude","CAP_FACE",FACE,{"disambiguationData":[OSD([sQuery(id+"F0.wireOp",EDGE,"E11.top"),subQ0,sQuery(id+"F3.wireOp",EDGE,"E18"),sQuery(id+"F5.wireOp",EDGE,"E22"),subQ1])],"isStart":false})],"blendedInto":[makeQuery(id+"F6.opExtrude","CAP_FACE",FACE,{"disambiguationData":[OSD([sQuery(id+"F0.wireOp",EDGE,"E11.top"),subQ0,sQuery(id+"F3.wireOp",EDGE,"E18"),sQuery(id+"F5.wireOp",EDGE,"E22"),subQ1])],"isStart":false})]}),makeQuery(id+"F6.boolean.opBoolean","MERGE",FACE,{"derivedFrom":[makeQuery(id+"F4.opExtrude","SWEPT_FACE",FACE,{"disambiguationData":[OSD([subQ0])]}),makeQuery(id+"F6.opExtrude","SWEPT_FACE",FACE,{"disambiguationData":[OSD([subQ0])]})]})],"blendedInto":[makeQuery(id+"F6.boolean.opBoolean","MERGE",FACE,{"derivedFrom":[makeQuery(id+"F4.opExtrude","SWEPT_FACE",FACE,{"disambiguationData":[OSD([subQ0])]}),makeQuery(id+"F6.opExtrude","SWEPT_FACE",FACE,{"disambiguationData":[OSD([subQ0])]})]})]});}
            var Q21;
            Q21=makeQuery(id+"F6.opExtrude","CAP_EDGE",EDGE,{"disambiguationData":[OSD([sQuery(id+"F3.wireOp",EDGE,"E17")])],"isStart":false});
            var Q22;
            {var subQ0=sQuery(id+"F3.wireOp",EDGE,"E17");var subQ1=sQuery(id+"F5.wireOp",EDGE,"E22");Q22=makeQuery(id+"F8.opFillet","BLEND_EDGE",EDGE,{"blendedFrom":[makeQuery(id+"F7.opChamfer","BLEND_EDGE",EDGE,{"blendedFrom":[makeQuery(id+"F6.opExtrude","CAP_EDGE",EDGE,{"disambiguationData":[OSD([subQ1])],"isStart":false}),makeQuery(id+"F6.opExtrude","CAP_FACE",FACE,{"disambiguationData":[OSD([sQuery(id+"F0.wireOp",EDGE,"E11.top"),subQ0,sQuery(id+"F3.wireOp",EDGE,"E18"),subQ1,sQuery(id+"F5.wireOp",EDGE,"E23")])],"isStart":false})],"blendedInto":[makeQuery(id+"F6.opExtrude","CAP_FACE",FACE,{"disambiguationData":[OSD([sQuery(id+"F0.wireOp",EDGE,"E11.top"),subQ0,sQuery(id+"F3.wireOp",EDGE,"E18"),subQ1,sQuery(id+"F5.wireOp",EDGE,"E23")])],"isStart":false})]}),makeQuery(id+"F6.boolean.opBoolean","MERGE",FACE,{"derivedFrom":[makeQuery(id+"F4.opExtrude","SWEPT_FACE",FACE,{"disambiguationData":[OSD([subQ0])]}),makeQuery(id+"F6.opExtrude","SWEPT_FACE",FACE,{"disambiguationData":[OSD([subQ0])]})]})],"blendedInto":[makeQuery(id+"F6.boolean.opBoolean","MERGE",FACE,{"derivedFrom":[makeQuery(id+"F4.opExtrude","SWEPT_FACE",FACE,{"disambiguationData":[OSD([subQ0])]}),makeQuery(id+"F6.opExtrude","SWEPT_FACE",FACE,{"disambiguationData":[OSD([subQ0])]})]})]});}
            var Q23;
            {var subQ0=sQuery(id+"F3.wireOp",EDGE,"E17");var subQ1=makeQuery(id+"F6.opExtrude","SWEPT_FACE",FACE,{"disambiguationData":[OSD([subQ0])]});var subQ2=makeQuery(id+"F4.opExtrude","SWEPT_FACE",FACE,{"disambiguationData":[OSD([subQ0])]});var subQ3=sQuery(id+"F0.wireOp",EDGE,"E11.right");var subQ4=sQuery(id+"F0.wireOp",EDGE,"E11.left");var subQ5=sQuery(id+"F0.wireOp",EDGE,"E11.top");var subQ6=sQuery(id+"F0.wireOp",EDGE,"E11.bottom");var subQ7=sQuery(id+"F0.wireOp",EDGE,"E10");var subQ8=sQuery(id+"F0.wireOp",EDGE,"E9");var subQ9=sQuery(id+"F0.wireOp",EDGE,"E0.right");var subQ10=sQuery(id+"F0.wireOp",EDGE,"E0.left");var subQ11=sQuery(id+"F0.wireOp",EDGE,"E0.top");var subQ12=sQuery(id+"F0.wireOp",EDGE,"E0.bottom");var subQ15=sQuery(id+"F3.wireOp",EDGE,"E18");var subQ16=sQuery(id+"F3.wireOp",EDGE,"E13");var subQ19=sQuery(id+"F5.wireOp",EDGE,"E22");Q23=makeQuery(id+"F9.opFillet","BLEND_EDGE",EDGE,{"blendedFrom":[makeQuery(id+"F7.opChamfer","BLEND_EDGE",EDGE,{"blendedFrom":[makeQuery(id+"F6.opExtrude","CAP_EDGE",EDGE,{"disambiguationData":[OSD([subQ19])],"isStart":false}),makeQuery(id+"F6.boolean.opBoolean","SPLIT",FACE,{"disambiguationData":[TD([subQ2])],"derivedFrom":makeQuery(id+"F4.opExtrude","CAP_FACE",FACE,{"disambiguationData":[OSD([subQ12,subQ11,subQ10,subQ9,subQ8,subQ7,subQ6,subQ5,subQ4,subQ3,subQ16,sQuery(id+"F3.wireOp",EDGE,"E16"),subQ0,subQ15,sQuery(id+"F3.wireOp",EDGE,"E19")])],"isStart":false})})],"blendedInto":[makeQuery(id+"F6.boolean.opBoolean","SPLIT",FACE,{"disambiguationData":[TD([subQ2])],"derivedFrom":makeQuery(id+"F4.opExtrude","CAP_FACE",FACE,{"disambiguationData":[OSD([subQ12,subQ11,subQ10,subQ9,subQ8,subQ7,subQ6,subQ5,subQ4,subQ3,subQ16,sQuery(id+"F3.wireOp",EDGE,"E16"),subQ0,subQ15,sQuery(id+"F3.wireOp",EDGE,"E19")])],"isStart":false})})]}),makeQuery(id+"F6.boolean.opBoolean","MERGE",FACE,{"derivedFrom":[subQ2,subQ1]})],"blendedInto":[makeQuery(id+"F6.boolean.opBoolean","MERGE",FACE,{"derivedFrom":[subQ2,subQ1]})]});}
            var Q24;
            Q24=makeQuery(id+"F4.opExtrude","CAP_EDGE",EDGE,{"disambiguationData":[OSD([sQuery(id+"F3.wireOp",EDGE,"E17")])],"isStart":false});
            var Q25;
            {var subQ0=sQuery(id+"F0.wireOp",EDGE,"E11.right");var subQ1=sQuery(id+"F0.wireOp",EDGE,"E11.left");var subQ2=sQuery(id+"F0.wireOp",EDGE,"E11.top");var subQ3=sQuery(id+"F0.wireOp",EDGE,"E11.bottom");var subQ4=sQuery(id+"F0.wireOp",EDGE,"E10");var subQ5=sQuery(id+"F0.wireOp",EDGE,"E9");var subQ6=sQuery(id+"F0.wireOp",EDGE,"E0.right");var subQ7=sQuery(id+"F0.wireOp",EDGE,"E0.left");var subQ8=sQuery(id+"F0.wireOp",EDGE,"E0.top");var subQ9=sQuery(id+"F0.wireOp",EDGE,"E0.bottom");Q25=makeQuery(id+"F4.opExtrude","CAP_EDGE",EDGE,{"disambiguationData":[OSD([subQ9,subQ8,subQ7,subQ6,subQ5,subQ4,subQ3,subQ2,subQ1,subQ0]),TDD([makeQuery(id+"F3.imprint","IMPRINT",EDGE,{"derivedFrom":makeQuery(id+"F2.opFillet","BLEND_EDGE",EDGE,{"blendedFrom":[makeQuery(id+"F1.opExtrude","CAP_EDGE",EDGE,{"disambiguationData":[OSD([subQ6])],"isStart":false}),makeQuery(id+"F1.opExtrude","CAP_FACE",FACE,{"disambiguationData":[OSD([subQ9,subQ8,subQ7,subQ6,subQ5,subQ4,subQ3,subQ2,subQ1,subQ0])],"isStart":false})],"blendedInto":[makeQuery(id+"F1.opExtrude","CAP_FACE",FACE,{"disambiguationData":[OSD([subQ9,subQ8,subQ7,subQ6,subQ5,subQ4,subQ3,subQ2,subQ1,subQ0])],"isStart":false})]})})])],"isStart":false});}
            var Q26;
            {var subQ0=sQuery(id+"F0.wireOp",EDGE,"E11.right");var subQ1=sQuery(id+"F0.wireOp",EDGE,"E11.left");var subQ2=sQuery(id+"F0.wireOp",EDGE,"E11.top");var subQ3=sQuery(id+"F0.wireOp",EDGE,"E11.bottom");var subQ4=sQuery(id+"F0.wireOp",EDGE,"E10");var subQ5=sQuery(id+"F0.wireOp",EDGE,"E9");var subQ6=sQuery(id+"F0.wireOp",EDGE,"E0.right");var subQ7=sQuery(id+"F0.wireOp",EDGE,"E0.left");var subQ8=sQuery(id+"F0.wireOp",EDGE,"E0.top");var subQ9=sQuery(id+"F0.wireOp",EDGE,"E0.bottom");Q26=makeQuery(id+"F4.opExtrude","CAP_EDGE",EDGE,{"disambiguationData":[OSD([subQ9,subQ8,subQ7,subQ6,subQ5,subQ4,subQ3,subQ2,subQ1,subQ0]),TDD([makeQuery(id+"F3.imprint","IMPRINT",EDGE,{"derivedFrom":makeQuery(id+"F2.opFillet","BLEND_EDGE",EDGE,{"blendedFrom":[makeQuery(id+"F1.opExtrude","CAP_EDGE",EDGE,{"disambiguationData":[OSD([subQ7])],"isStart":false}),makeQuery(id+"F1.opExtrude","CAP_FACE",FACE,{"disambiguationData":[OSD([subQ9,subQ8,subQ7,subQ6,subQ5,subQ4,subQ3,subQ2,subQ1,subQ0])],"isStart":false})],"blendedInto":[makeQuery(id+"F1.opExtrude","CAP_FACE",FACE,{"disambiguationData":[OSD([subQ9,subQ8,subQ7,subQ6,subQ5,subQ4,subQ3,subQ2,subQ1,subQ0])],"isStart":false})]})})])],"isStart":false});}
            var Q27;
            Q27=makeQuery(id+"F4.opExtrude","CAP_EDGE",EDGE,{"disambiguationData":[OSD([sQuery(id+"F3.wireOp",EDGE,"E21")])],"isStart":false});
            var Q28;
            Q28=makeQuery(id+"F4.opExtrude","CAP_EDGE",EDGE,{"disambiguationData":[OSD([sQuery(id+"F3.wireOp",EDGE,"E20")])],"isStart":false});
            fillet(context, id + "F10", {"entities" : qUnion([Q0, Q1, Q2, Q3, Q4, Q5, Q6, Q7, Q8, Q9, Q10, Q11, Q12, Q13, Q14, Q15, Q16, Q17, Q18, Q19, Q20, Q21, Q22, Q23, Q24, Q25, Q26, Q27, Q28]), "radius" : 1 * mm, "tangentPropagation" : true, "allowEdgeOverflow" : false});
        }
    });
